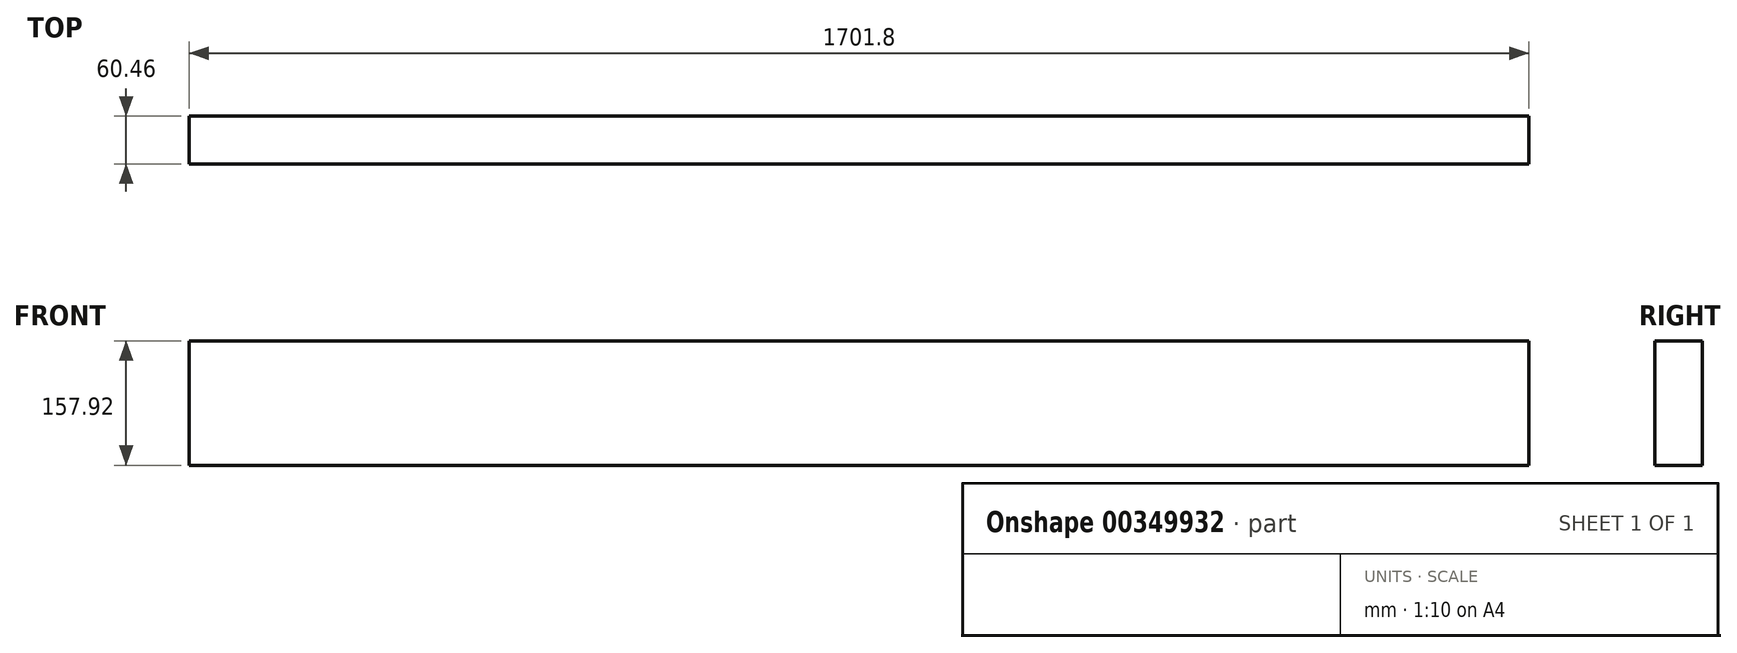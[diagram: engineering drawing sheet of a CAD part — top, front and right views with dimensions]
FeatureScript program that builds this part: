
annotation { "Feature Type Name" : "Feature", "Feature Type Description" : "" }
export const myFeature = defineFeature(function(context is Context, id is Id, definition is map)
    precondition{}
    {
        {
            var Q0;
            Q0=qCreatedBy(makeId("Right.planeOp"),FACE);
            var sketch = newSketch(context, id + "F0", { "sketchPlane" : qUnion([Q0])});
            skLineSegment(sketch, "E0.bottom", {"start": v(-30.23, -78.96) * mm, "end": v(30.23, -78.96) * mm});
            skLineSegment(sketch, "E0.top", {"start": v(-30.23, 78.96) * mm, "end": v(30.23, 78.96) * mm});
            skLineSegment(sketch, "E0.left", {"start": v(-30.23, -78.96) * mm, "end": v(-30.23, 78.96) * mm});
            skLineSegment(sketch, "E0.right", {"start": v(30.23, -78.96) * mm, "end": v(30.23, 78.96) * mm});
            skPoint(sketch, "E0.middle", {"position": v(0, 0) * mm});
            skSolve(sketch);
        }
        {
            var Q0;
            Q0 = qSketchRegion(id + "F0", true);
            extrude(context, id + "F1", {"entities" : qUnion([Q0]), "depth" : 1701.8 * mm, "offsetDistance" : 25.4 * mm});
        }
    });
